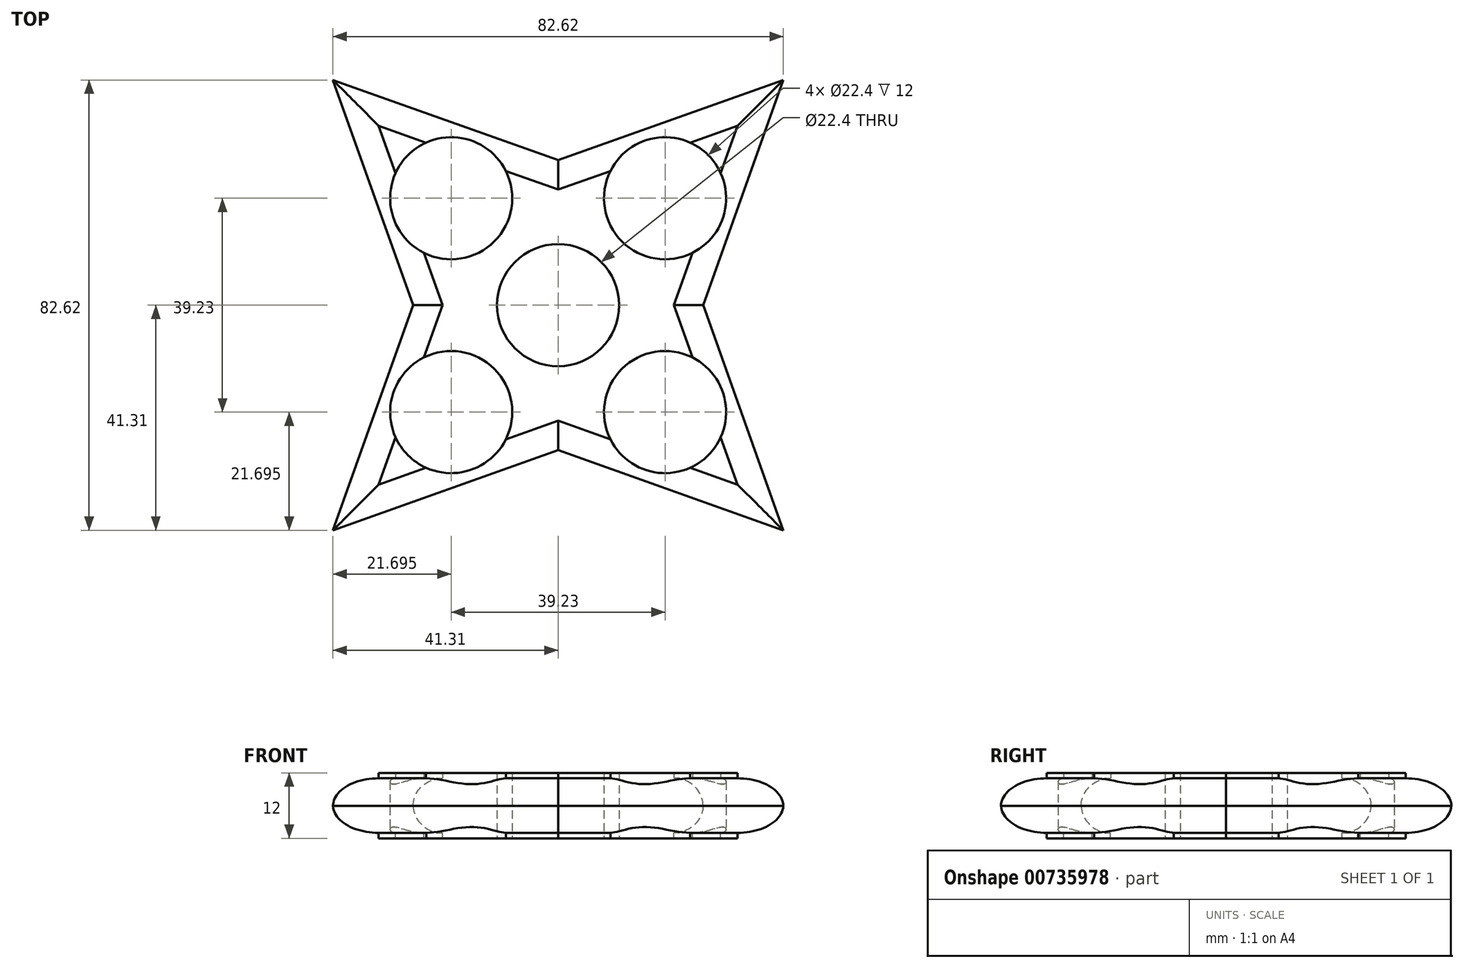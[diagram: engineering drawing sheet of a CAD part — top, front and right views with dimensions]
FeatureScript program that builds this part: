
annotation { "Feature Type Name" : "Feature", "Feature Type Description" : "" }
export const myFeature = defineFeature(function(context is Context, id is Id, definition is map)
    precondition{}
    {
        {
            var Q0;
            Q0=qCreatedBy(makeId("Top.planeOp"),FACE);
            var sketch = newSketch(context, id + "F0", { "sketchPlane" : qUnion([Q0])});
            skLineSegment(sketch, "E0.bottom", {"start": v(-109.63, 111.87) * mm, "end": v(113.44, 111.87) * mm});
            skLineSegment(sketch, "E0.top", {"start": v(-109.63, -97) * mm, "end": v(113.44, -97) * mm});
            skLineSegment(sketch, "E0.left", {"start": v(-109.63, 111.87) * mm, "end": v(-109.63, -97) * mm});
            skLineSegment(sketch, "E0.right", {"start": v(113.44, 111.87) * mm, "end": v(113.44, -97) * mm});
            skCircle(sketch, "E1", {"center": v(0, 0) * mm, "radius": 11.2 * mm});
            skLineSegment(sketch, "E2", {"start": v(0, 11.2) * mm, "end": v(0, 74.7) * mm});
            skLineSegment(sketch, "E3", {"start": v(11.2, 0) * mm, "end": v(74.7, 0) * mm});
            skLineSegment(sketch, "E4", {"start": v(0, -11.2) * mm, "end": v(0, -74.7) * mm});
            skLineSegment(sketch, "E5", {"start": v(-11.2, 0) * mm, "end": v(-74.7, 0) * mm});
            skLineSegment(sketch, "E6", {"start": v(41.3, 41.3) * mm, "end": v(0, -74.7) * mm});
            skLineSegment(sketch, "E7", {"start": v(-41.3, 41.3) * mm, "end": v(0, -74.7) * mm});
            skLineSegment(sketch, "E8", {"start": v(-74.7, 0) * mm, "end": v(41.3, 41.3) * mm});
            skLineSegment(sketch, "E9", {"start": v(41.3, -41.3) * mm, "end": v(-74.7, 0) * mm});
            skLineSegment(sketch, "E10", {"start": v(-41.3, -41.3) * mm, "end": v(0, 74.7) * mm});
            skLineSegment(sketch, "E11", {"start": v(41.3, -41.3) * mm, "end": v(0, 74.7) * mm});
            skLineSegment(sketch, "E12", {"start": v(-41.3, -41.3) * mm, "end": v(74.7, 0) * mm});
            skLineSegment(sketch, "E13", {"start": v(-41.3, 41.3) * mm, "end": v(74.7, 0) * mm});
            skLineSegment(sketch, "E14", {"start": v(0, 0) * mm, "end": v(-41.3, -41.3) * mm});
            skLineSegment(sketch, "E15", {"start": v(0, 0) * mm, "end": v(41.3, 41.3) * mm});
            skLineSegment(sketch, "E16", {"start": v(0, 0) * mm, "end": v(-41.3, 41.3) * mm});
            skLineSegment(sketch, "E17", {"start": v(0, 0) * mm, "end": v(41.3, -41.3) * mm});
            skCircle(sketch, "E18", {"center": v(-19.61, 19.61) * mm, "radius": 11.2 * mm});
            skCircle(sketch, "E19", {"center": v(19.61, 19.61) * mm, "radius": 11.2 * mm});
            skCircle(sketch, "E20", {"center": v(-19.61, -19.61) * mm, "radius": 11.2 * mm});
            skCircle(sketch, "E21", {"center": v(19.61, -19.61) * mm, "radius": 11.2 * mm});
            skSolve(sketch);
        }
        {
            var Q0;
            {var subQ0=sQuery(id+"F0.wireOp",EDGE,"E9");var subQ1=sQuery(id+"F0.wireOp",EDGE,"E6");var subQ2=makeQuery(id+"F0.imprint","INTERSECT",VERTEX,{"derivedFrom":[subQ1,subQ0]});Q0=makeQuery(id+"F0.imprint","IMPRINT",FACE,{"disambiguationData":[TD([[makeQuery(id+"F0.imprint","IMPRINT",EDGE,{"disambiguationData":[TD([[subQ2,1.0]])],"derivedFrom":subQ1}),-1.0]])]});}
            var Q1;
            {var subQ0=sQuery(id+"F0.wireOp",EDGE,"E12");var subQ1=sQuery(id+"F0.wireOp",EDGE,"E7");var subQ2=makeQuery(id+"F0.imprint","INTERSECT",VERTEX,{"derivedFrom":[subQ1,subQ0]});Q1=makeQuery(id+"F0.imprint","IMPRINT",FACE,{"disambiguationData":[TD([[makeQuery(id+"F0.imprint","IMPRINT",EDGE,{"disambiguationData":[TD([[subQ2,1.0]])],"derivedFrom":subQ1}),1.0]])]});}
            var Q2;
            {var subQ0=sQuery(id+"F0.wireOp",EDGE,"E4");var subQ1=sQuery(id+"F0.wireOp",EDGE,"E1");var subQ2=makeQuery(id+"F0.imprint","INTERSECT",VERTEX,{"derivedFrom":[subQ1,subQ0]});Q2=makeQuery(id+"F0.imprint","IMPRINT",FACE,{"disambiguationData":[TD([[makeQuery(id+"F0.imprint","IMPRINT",EDGE,{"disambiguationData":[TD([[subQ2,1.0]])],"derivedFrom":subQ1}),-1.0]])]});}
            var Q3;
            {var subQ0=sQuery(id+"F0.wireOp",EDGE,"E5");var subQ1=sQuery(id+"F0.wireOp",EDGE,"E1");var subQ2=makeQuery(id+"F0.imprint","INTERSECT",VERTEX,{"derivedFrom":[subQ1,subQ0]});Q3=makeQuery(id+"F0.imprint","IMPRINT",FACE,{"disambiguationData":[TD([[makeQuery(id+"F0.imprint","IMPRINT",EDGE,{"disambiguationData":[TD([[subQ2,-1.0]])],"derivedFrom":subQ1}),-1.0]])]});}
            var Q4;
            {var subQ0=sQuery(id+"F0.wireOp",EDGE,"E5");var subQ1=sQuery(id+"F0.wireOp",EDGE,"E1");var subQ2=makeQuery(id+"F0.imprint","INTERSECT",VERTEX,{"derivedFrom":[subQ1,subQ0]});Q4=makeQuery(id+"F0.imprint","IMPRINT",FACE,{"disambiguationData":[TD([[makeQuery(id+"F0.imprint","IMPRINT",EDGE,{"disambiguationData":[TD([[subQ2,1.0]])],"derivedFrom":subQ1}),-1.0]])]});}
            var Q5;
            {var subQ0=sQuery(id+"F0.wireOp",EDGE,"E2");var subQ1=sQuery(id+"F0.wireOp",EDGE,"E1");var subQ2=makeQuery(id+"F0.imprint","INTERSECT",VERTEX,{"derivedFrom":[subQ1,subQ0]});Q5=makeQuery(id+"F0.imprint","IMPRINT",FACE,{"disambiguationData":[TD([[makeQuery(id+"F0.imprint","IMPRINT",EDGE,{"disambiguationData":[TD([[subQ2,-1.0]])],"derivedFrom":subQ1}),-1.0]])]});}
            var Q6;
            {var subQ0=sQuery(id+"F0.wireOp",EDGE,"E2");var subQ1=sQuery(id+"F0.wireOp",EDGE,"E1");var subQ2=makeQuery(id+"F0.imprint","INTERSECT",VERTEX,{"derivedFrom":[subQ1,subQ0]});Q6=makeQuery(id+"F0.imprint","IMPRINT",FACE,{"disambiguationData":[TD([[makeQuery(id+"F0.imprint","IMPRINT",EDGE,{"disambiguationData":[TD([[subQ2,1.0]])],"derivedFrom":subQ1}),-1.0]])]});}
            var Q7;
            {var subQ0=sQuery(id+"F0.wireOp",EDGE,"E3");var subQ1=sQuery(id+"F0.wireOp",EDGE,"E1");var subQ2=makeQuery(id+"F0.imprint","INTERSECT",VERTEX,{"derivedFrom":[subQ1,subQ0]});Q7=makeQuery(id+"F0.imprint","IMPRINT",FACE,{"disambiguationData":[TD([[makeQuery(id+"F0.imprint","IMPRINT",EDGE,{"disambiguationData":[TD([[subQ2,-1.0]])],"derivedFrom":subQ1}),-1.0]])]});}
            var Q8;
            {var subQ0=sQuery(id+"F0.wireOp",EDGE,"E3");var subQ1=sQuery(id+"F0.wireOp",EDGE,"E1");var subQ2=makeQuery(id+"F0.imprint","INTERSECT",VERTEX,{"derivedFrom":[subQ1,subQ0]});Q8=makeQuery(id+"F0.imprint","IMPRINT",FACE,{"disambiguationData":[TD([[makeQuery(id+"F0.imprint","IMPRINT",EDGE,{"disambiguationData":[TD([[subQ2,1.0]])],"derivedFrom":subQ1}),-1.0]])]});}
            var Q9;
            {var subQ0=sQuery(id+"F0.wireOp",EDGE,"E4");var subQ1=sQuery(id+"F0.wireOp",EDGE,"E1");var subQ2=makeQuery(id+"F0.imprint","INTERSECT",VERTEX,{"derivedFrom":[subQ1,subQ0]});Q9=makeQuery(id+"F0.imprint","IMPRINT",FACE,{"disambiguationData":[TD([[makeQuery(id+"F0.imprint","IMPRINT",EDGE,{"disambiguationData":[TD([[subQ2,-1.0]])],"derivedFrom":subQ1}),-1.0]])]});}
            var Q10;
            {var subQ0=sQuery(id+"F0.wireOp",EDGE,"E11");var subQ3=sQuery(id+"F0.wireOp",EDGE,"E12");var subQ5=makeQuery(id+"F0.imprint","INTERSECT",VERTEX,{"derivedFrom":[subQ0,subQ3]});Q10=makeQuery(id+"F0.imprint","IMPRINT",FACE,{"disambiguationData":[TD([[makeQuery(id+"F0.imprint","IMPRINT",EDGE,{"disambiguationData":[TD([[subQ5,-1.0]])],"derivedFrom":subQ0}),1.0]])]});}
            var Q11;
            {var subQ0=sQuery(id+"F0.wireOp",EDGE,"E13");var subQ1=sQuery(id+"F0.wireOp",EDGE,"E6");var subQ2=makeQuery(id+"F0.imprint","INTERSECT",VERTEX,{"derivedFrom":[subQ1,subQ0]});Q11=makeQuery(id+"F0.imprint","IMPRINT",FACE,{"disambiguationData":[TD([[makeQuery(id+"F0.imprint","IMPRINT",EDGE,{"disambiguationData":[TD([[subQ2,-1.0]])],"derivedFrom":subQ1}),-1.0]])]});}
            var Q12;
            {var subQ0=sQuery(id+"F0.wireOp",EDGE,"E13");var subQ3=sQuery(id+"F0.wireOp",EDGE,"E10");var subQ5=makeQuery(id+"F0.imprint","INTERSECT",VERTEX,{"derivedFrom":[subQ3,subQ0]});Q12=makeQuery(id+"F0.imprint","IMPRINT",FACE,{"disambiguationData":[TD([[makeQuery(id+"F0.imprint","IMPRINT",EDGE,{"disambiguationData":[TD([[subQ5,1.0]])],"derivedFrom":subQ3}),-1.0]])]});}
            var Q13;
            {var subQ0=sQuery(id+"F0.wireOp",EDGE,"E11");var subQ1=sQuery(id+"F0.wireOp",EDGE,"E8");var subQ2=makeQuery(id+"F0.imprint","INTERSECT",VERTEX,{"derivedFrom":[subQ1,subQ0]});Q13=makeQuery(id+"F0.imprint","IMPRINT",FACE,{"disambiguationData":[TD([[makeQuery(id+"F0.imprint","IMPRINT",EDGE,{"disambiguationData":[TD([[subQ2,1.0]])],"derivedFrom":subQ1}),-1.0]])]});}
            var Q14;
            {var subQ0=sQuery(id+"F0.wireOp",EDGE,"E8");var subQ3=sQuery(id+"F0.wireOp",EDGE,"E11");var subQ5=makeQuery(id+"F0.imprint","INTERSECT",VERTEX,{"derivedFrom":[subQ0,subQ3]});Q14=makeQuery(id+"F0.imprint","IMPRINT",FACE,{"disambiguationData":[TD([[makeQuery(id+"F0.imprint","IMPRINT",EDGE,{"disambiguationData":[TD([[subQ5,-1.0]])],"derivedFrom":subQ0}),-1.0]])]});}
            var Q15;
            {var subQ0=sQuery(id+"F0.wireOp",EDGE,"E6");var subQ3=sQuery(id+"F0.wireOp",EDGE,"E13");var subQ5=makeQuery(id+"F0.imprint","INTERSECT",VERTEX,{"derivedFrom":[subQ0,subQ3]});Q15=makeQuery(id+"F0.imprint","IMPRINT",FACE,{"disambiguationData":[TD([[makeQuery(id+"F0.imprint","IMPRINT",EDGE,{"disambiguationData":[TD([[subQ5,1.0]])],"derivedFrom":subQ0}),-1.0]])]});}
            var Q16;
            {var subQ0=sQuery(id+"F0.wireOp",EDGE,"E9");var subQ3=sQuery(id+"F0.wireOp",EDGE,"E6");var subQ5=makeQuery(id+"F0.imprint","INTERSECT",VERTEX,{"derivedFrom":[subQ3,subQ0]});Q16=makeQuery(id+"F0.imprint","IMPRINT",FACE,{"disambiguationData":[TD([[makeQuery(id+"F0.imprint","IMPRINT",EDGE,{"disambiguationData":[TD([[subQ5,1.0]])],"derivedFrom":subQ3}),1.0]])]});}
            var Q17;
            {var subQ0=sQuery(id+"F0.wireOp",EDGE,"E11");var subQ3=sQuery(id+"F0.wireOp",EDGE,"E12");var subQ5=makeQuery(id+"F0.imprint","INTERSECT",VERTEX,{"derivedFrom":[subQ0,subQ3]});Q17=makeQuery(id+"F0.imprint","IMPRINT",FACE,{"disambiguationData":[TD([[makeQuery(id+"F0.imprint","IMPRINT",EDGE,{"disambiguationData":[TD([[subQ5,1.0]])],"derivedFrom":subQ0}),1.0]])]});}
            var Q18;
            {var subQ0=sQuery(id+"F0.wireOp",EDGE,"E12");var subQ3=sQuery(id+"F0.wireOp",EDGE,"E7");var subQ5=makeQuery(id+"F0.imprint","INTERSECT",VERTEX,{"derivedFrom":[subQ3,subQ0]});Q18=makeQuery(id+"F0.imprint","IMPRINT",FACE,{"disambiguationData":[TD([[makeQuery(id+"F0.imprint","IMPRINT",EDGE,{"disambiguationData":[TD([[subQ5,1.0]])],"derivedFrom":subQ3}),-1.0]])]});}
            var Q19;
            {var subQ0=sQuery(id+"F0.wireOp",EDGE,"E10");var subQ3=sQuery(id+"F0.wireOp",EDGE,"E9");var subQ5=makeQuery(id+"F0.imprint","INTERSECT",VERTEX,{"derivedFrom":[subQ3,subQ0]});Q19=makeQuery(id+"F0.imprint","IMPRINT",FACE,{"disambiguationData":[TD([[makeQuery(id+"F0.imprint","IMPRINT",EDGE,{"disambiguationData":[TD([[subQ5,1.0]])],"derivedFrom":subQ3}),-1.0]])]});}
            var Q20;
            {var subQ0=sQuery(id+"F0.wireOp",EDGE,"E10");var subQ3=sQuery(id+"F0.wireOp",EDGE,"E9");var subQ5=makeQuery(id+"F0.imprint","INTERSECT",VERTEX,{"derivedFrom":[subQ3,subQ0]});Q20=makeQuery(id+"F0.imprint","IMPRINT",FACE,{"disambiguationData":[TD([[makeQuery(id+"F0.imprint","IMPRINT",EDGE,{"disambiguationData":[TD([[subQ5,1.0]])],"derivedFrom":subQ3}),1.0]])]});}
            var Q21;
            {var subQ0=sQuery(id+"F0.wireOp",EDGE,"E8");var subQ1=sQuery(id+"F0.wireOp",EDGE,"E7");var subQ2=makeQuery(id+"F0.imprint","INTERSECT",VERTEX,{"derivedFrom":[subQ1,subQ0]});Q21=makeQuery(id+"F0.imprint","IMPRINT",FACE,{"disambiguationData":[TD([[makeQuery(id+"F0.imprint","IMPRINT",EDGE,{"disambiguationData":[TD([[subQ2,-1.0]])],"derivedFrom":subQ1}),1.0]])]});}
            var Q22;
            {var subQ0=sQuery(id+"F0.wireOp",EDGE,"E7");var subQ3=sQuery(id+"F0.wireOp",EDGE,"E8");var subQ5=makeQuery(id+"F0.imprint","INTERSECT",VERTEX,{"derivedFrom":[subQ0,subQ3]});Q22=makeQuery(id+"F0.imprint","IMPRINT",FACE,{"disambiguationData":[TD([[makeQuery(id+"F0.imprint","IMPRINT",EDGE,{"disambiguationData":[TD([[subQ5,1.0]])],"derivedFrom":subQ0}),1.0]])]});}
            var Q23;
            {var subQ0=sQuery(id+"F0.wireOp",EDGE,"E13");var subQ3=sQuery(id+"F0.wireOp",EDGE,"E10");var subQ5=makeQuery(id+"F0.imprint","INTERSECT",VERTEX,{"derivedFrom":[subQ3,subQ0]});Q23=makeQuery(id+"F0.imprint","IMPRINT",FACE,{"disambiguationData":[TD([[makeQuery(id+"F0.imprint","IMPRINT",EDGE,{"disambiguationData":[TD([[subQ5,1.0]])],"derivedFrom":subQ3}),1.0]])]});}
            extrude(context, id + "F1", {"entities" : qUnion([Q0, Q1, Q2, Q3, Q4, Q5, Q6, Q7, Q8, Q9, Q10, Q11, Q12, Q13, Q14, Q15, Q16, Q17, Q18, Q19, Q20, Q21, Q22, Q23]), "depth" : 10 * mm, "offsetDistance" : 25.4 * mm});
        }
        {
            var Q0;
            Q0=makeQuery(id+"F1.opExtrude","CAP_EDGE",EDGE,{"disambiguationData":[OSD([sQuery(id+"F0.wireOp",EDGE,"E10")])],"isStart":false});
            var Q1;
            Q1=makeQuery(id+"F1.opExtrude","CAP_EDGE",EDGE,{"disambiguationData":[OSD([sQuery(id+"F0.wireOp",EDGE,"E7")])],"isStart":false});
            var Q2;
            Q2=makeQuery(id+"F1.opExtrude","CAP_EDGE",EDGE,{"disambiguationData":[OSD([sQuery(id+"F0.wireOp",EDGE,"E12")])],"isStart":false});
            var Q3;
            Q3=makeQuery(id+"F1.opExtrude","CAP_EDGE",EDGE,{"disambiguationData":[OSD([sQuery(id+"F0.wireOp",EDGE,"E9")])],"isStart":false});
            var Q4;
            Q4=makeQuery(id+"F1.opExtrude","CAP_EDGE",EDGE,{"disambiguationData":[OSD([sQuery(id+"F0.wireOp",EDGE,"E11")])],"isStart":false});
            var Q5;
            Q5=makeQuery(id+"F1.opExtrude","CAP_EDGE",EDGE,{"disambiguationData":[OSD([sQuery(id+"F0.wireOp",EDGE,"E6")])],"isStart":false});
            var Q6;
            Q6=makeQuery(id+"F1.opExtrude","CAP_EDGE",EDGE,{"disambiguationData":[OSD([sQuery(id+"F0.wireOp",EDGE,"E8")])],"isStart":false});
            var Q7;
            Q7=makeQuery(id+"F1.opExtrude","CAP_EDGE",EDGE,{"disambiguationData":[OSD([sQuery(id+"F0.wireOp",EDGE,"E13")])],"isStart":false});
            fillet(context, id + "F2", {"entities" : qUnion([Q0, Q1, Q2, Q3, Q4, Q5, Q6, Q7]), "radius" : 5.08 * mm, "tangentPropagation" : true, "allowEdgeOverflow" : false});
        }
        {
            var Q0;
            Q0=makeQuery(id+"F1.opExtrude","CAP_EDGE",EDGE,{"disambiguationData":[OSD([sQuery(id+"F0.wireOp",EDGE,"E8")])],"isStart":true});
            var Q1;
            Q1=makeQuery(id+"F1.opExtrude","CAP_EDGE",EDGE,{"disambiguationData":[OSD([sQuery(id+"F0.wireOp",EDGE,"E6")])],"isStart":true});
            var Q2;
            Q2=makeQuery(id+"F1.opExtrude","CAP_EDGE",EDGE,{"disambiguationData":[OSD([sQuery(id+"F0.wireOp",EDGE,"E11")])],"isStart":true});
            var Q3;
            Q3=makeQuery(id+"F1.opExtrude","CAP_EDGE",EDGE,{"disambiguationData":[OSD([sQuery(id+"F0.wireOp",EDGE,"E9")])],"isStart":true});
            var Q4;
            Q4=makeQuery(id+"F1.opExtrude","CAP_EDGE",EDGE,{"disambiguationData":[OSD([sQuery(id+"F0.wireOp",EDGE,"E12")])],"isStart":true});
            var Q5;
            Q5=makeQuery(id+"F1.opExtrude","CAP_EDGE",EDGE,{"disambiguationData":[OSD([sQuery(id+"F0.wireOp",EDGE,"E10")])],"isStart":true});
            var Q6;
            Q6=makeQuery(id+"F1.opExtrude","CAP_EDGE",EDGE,{"disambiguationData":[OSD([sQuery(id+"F0.wireOp",EDGE,"E7")])],"isStart":true});
            var Q7;
            Q7=makeQuery(id+"F1.opExtrude","CAP_EDGE",EDGE,{"disambiguationData":[OSD([sQuery(id+"F0.wireOp",EDGE,"E13")])],"isStart":true});
            fillet(context, id + "F3", {"entities" : qUnion([Q0, Q1, Q2, Q3, Q4, Q5, Q6, Q7]), "radius" : 5.08 * mm, "tangentPropagation" : true, "allowEdgeOverflow" : false});
        }
        {
            var Q0;
            Q0=makeQuery(id+"F2.opFillet","SPLIT",FACE,{"disambiguationData":[OD(2.0)],"derivedFrom":makeQuery(id+"F1.opExtrude","CAP_FACE",FACE,{"disambiguationData":[OSD([sQuery(id+"F0.wireOp",EDGE,"E1"),sQuery(id+"F0.wireOp",EDGE,"E6"),sQuery(id+"F0.wireOp",EDGE,"E7"),sQuery(id+"F0.wireOp",EDGE,"E8"),sQuery(id+"F0.wireOp",EDGE,"E9"),sQuery(id+"F0.wireOp",EDGE,"E10"),sQuery(id+"F0.wireOp",EDGE,"E11"),sQuery(id+"F0.wireOp",EDGE,"E12"),sQuery(id+"F0.wireOp",EDGE,"E13"),sQuery(id+"F0.wireOp",EDGE,"NQLChufh-tOBQ-VhrW-I5os-LazHDcaticKj"),sQuery(id+"F0.wireOp",EDGE,"nPcMzMfi-i0d1-RiFT-5sVm-fAcf6640eUi0"),sQuery(id+"F0.wireOp",EDGE,"xpLk3V2d-4zdc-2TxM-j6uB-WA1YDWCwNWJT"),sQuery(id+"F0.wireOp",EDGE,"mvu3pI7v-0WKY-5XG3-tPVA-ciItBbTbTf2v")])],"isStart":false})});
            var Q1;
            Q1=makeQuery(id+"F2.opFillet","SPLIT",FACE,{"disambiguationData":[OD(1.0)],"derivedFrom":makeQuery(id+"F1.opExtrude","CAP_FACE",FACE,{"disambiguationData":[OSD([sQuery(id+"F0.wireOp",EDGE,"E1"),sQuery(id+"F0.wireOp",EDGE,"E6"),sQuery(id+"F0.wireOp",EDGE,"E7"),sQuery(id+"F0.wireOp",EDGE,"E8"),sQuery(id+"F0.wireOp",EDGE,"E9"),sQuery(id+"F0.wireOp",EDGE,"E10"),sQuery(id+"F0.wireOp",EDGE,"E11"),sQuery(id+"F0.wireOp",EDGE,"E12"),sQuery(id+"F0.wireOp",EDGE,"E13"),sQuery(id+"F0.wireOp",EDGE,"NQLChufh-tOBQ-VhrW-I5os-LazHDcaticKj"),sQuery(id+"F0.wireOp",EDGE,"nPcMzMfi-i0d1-RiFT-5sVm-fAcf6640eUi0"),sQuery(id+"F0.wireOp",EDGE,"xpLk3V2d-4zdc-2TxM-j6uB-WA1YDWCwNWJT"),sQuery(id+"F0.wireOp",EDGE,"mvu3pI7v-0WKY-5XG3-tPVA-ciItBbTbTf2v")])],"isStart":false})});
            var Q2;
            Q2=makeQuery(id+"F2.opFillet","SPLIT",FACE,{"disambiguationData":[OD(3.0)],"derivedFrom":makeQuery(id+"F1.opExtrude","CAP_FACE",FACE,{"disambiguationData":[OSD([sQuery(id+"F0.wireOp",EDGE,"E1"),sQuery(id+"F0.wireOp",EDGE,"E6"),sQuery(id+"F0.wireOp",EDGE,"E7"),sQuery(id+"F0.wireOp",EDGE,"E8"),sQuery(id+"F0.wireOp",EDGE,"E9"),sQuery(id+"F0.wireOp",EDGE,"E10"),sQuery(id+"F0.wireOp",EDGE,"E11"),sQuery(id+"F0.wireOp",EDGE,"E12"),sQuery(id+"F0.wireOp",EDGE,"E13"),sQuery(id+"F0.wireOp",EDGE,"NQLChufh-tOBQ-VhrW-I5os-LazHDcaticKj"),sQuery(id+"F0.wireOp",EDGE,"nPcMzMfi-i0d1-RiFT-5sVm-fAcf6640eUi0"),sQuery(id+"F0.wireOp",EDGE,"xpLk3V2d-4zdc-2TxM-j6uB-WA1YDWCwNWJT"),sQuery(id+"F0.wireOp",EDGE,"mvu3pI7v-0WKY-5XG3-tPVA-ciItBbTbTf2v")])],"isStart":false})});
            var Q3;
            Q3=makeQuery(id+"F2.opFillet","SPLIT",FACE,{"disambiguationData":[OD(0.0)],"derivedFrom":makeQuery(id+"F1.opExtrude","CAP_FACE",FACE,{"disambiguationData":[OSD([sQuery(id+"F0.wireOp",EDGE,"E1"),sQuery(id+"F0.wireOp",EDGE,"E6"),sQuery(id+"F0.wireOp",EDGE,"E7"),sQuery(id+"F0.wireOp",EDGE,"E8"),sQuery(id+"F0.wireOp",EDGE,"E9"),sQuery(id+"F0.wireOp",EDGE,"E10"),sQuery(id+"F0.wireOp",EDGE,"E11"),sQuery(id+"F0.wireOp",EDGE,"E12"),sQuery(id+"F0.wireOp",EDGE,"E13"),sQuery(id+"F0.wireOp",EDGE,"NQLChufh-tOBQ-VhrW-I5os-LazHDcaticKj"),sQuery(id+"F0.wireOp",EDGE,"nPcMzMfi-i0d1-RiFT-5sVm-fAcf6640eUi0"),sQuery(id+"F0.wireOp",EDGE,"xpLk3V2d-4zdc-2TxM-j6uB-WA1YDWCwNWJT"),sQuery(id+"F0.wireOp",EDGE,"mvu3pI7v-0WKY-5XG3-tPVA-ciItBbTbTf2v")])],"isStart":false})});
            var Q4;
            Q4=makeQuery(id+"F2.opFillet","SPLIT",FACE,{"disambiguationData":[OD(4.0)],"derivedFrom":makeQuery(id+"F1.opExtrude","CAP_FACE",FACE,{"disambiguationData":[OSD([sQuery(id+"F0.wireOp",EDGE,"E1"),sQuery(id+"F0.wireOp",EDGE,"E6"),sQuery(id+"F0.wireOp",EDGE,"E7"),sQuery(id+"F0.wireOp",EDGE,"E8"),sQuery(id+"F0.wireOp",EDGE,"E9"),sQuery(id+"F0.wireOp",EDGE,"E10"),sQuery(id+"F0.wireOp",EDGE,"E11"),sQuery(id+"F0.wireOp",EDGE,"E12"),sQuery(id+"F0.wireOp",EDGE,"E13"),sQuery(id+"F0.wireOp",EDGE,"NQLChufh-tOBQ-VhrW-I5os-LazHDcaticKj"),sQuery(id+"F0.wireOp",EDGE,"nPcMzMfi-i0d1-RiFT-5sVm-fAcf6640eUi0"),sQuery(id+"F0.wireOp",EDGE,"xpLk3V2d-4zdc-2TxM-j6uB-WA1YDWCwNWJT"),sQuery(id+"F0.wireOp",EDGE,"mvu3pI7v-0WKY-5XG3-tPVA-ciItBbTbTf2v")])],"isStart":false})});
            extrude(context, id + "F4", {"entities" : qUnion([Q0, Q1, Q2, Q3, Q4]), "operationType" : NewBodyOperationType.ADD, "depth" : 1 * mm, "offsetDistance" : 25.4 * mm});
        }
        {
            var Q0;
            Q0=makeQuery(id+"F3.opFillet","SPLIT",FACE,{"disambiguationData":[OD(2.0)],"derivedFrom":makeQuery(id+"F1.opExtrude","CAP_FACE",FACE,{"disambiguationData":[OSD([sQuery(id+"F0.wireOp",EDGE,"E1"),sQuery(id+"F0.wireOp",EDGE,"E6"),sQuery(id+"F0.wireOp",EDGE,"E7"),sQuery(id+"F0.wireOp",EDGE,"E8"),sQuery(id+"F0.wireOp",EDGE,"E9"),sQuery(id+"F0.wireOp",EDGE,"E10"),sQuery(id+"F0.wireOp",EDGE,"E11"),sQuery(id+"F0.wireOp",EDGE,"E12"),sQuery(id+"F0.wireOp",EDGE,"E13"),sQuery(id+"F0.wireOp",EDGE,"NQLChufh-tOBQ-VhrW-I5os-LazHDcaticKj"),sQuery(id+"F0.wireOp",EDGE,"nPcMzMfi-i0d1-RiFT-5sVm-fAcf6640eUi0"),sQuery(id+"F0.wireOp",EDGE,"xpLk3V2d-4zdc-2TxM-j6uB-WA1YDWCwNWJT"),sQuery(id+"F0.wireOp",EDGE,"mvu3pI7v-0WKY-5XG3-tPVA-ciItBbTbTf2v")])],"isStart":true})});
            var Q1;
            Q1=makeQuery(id+"F3.opFillet","SPLIT",FACE,{"disambiguationData":[OD(3.0)],"derivedFrom":makeQuery(id+"F1.opExtrude","CAP_FACE",FACE,{"disambiguationData":[OSD([sQuery(id+"F0.wireOp",EDGE,"E1"),sQuery(id+"F0.wireOp",EDGE,"E6"),sQuery(id+"F0.wireOp",EDGE,"E7"),sQuery(id+"F0.wireOp",EDGE,"E8"),sQuery(id+"F0.wireOp",EDGE,"E9"),sQuery(id+"F0.wireOp",EDGE,"E10"),sQuery(id+"F0.wireOp",EDGE,"E11"),sQuery(id+"F0.wireOp",EDGE,"E12"),sQuery(id+"F0.wireOp",EDGE,"E13"),sQuery(id+"F0.wireOp",EDGE,"NQLChufh-tOBQ-VhrW-I5os-LazHDcaticKj"),sQuery(id+"F0.wireOp",EDGE,"nPcMzMfi-i0d1-RiFT-5sVm-fAcf6640eUi0"),sQuery(id+"F0.wireOp",EDGE,"xpLk3V2d-4zdc-2TxM-j6uB-WA1YDWCwNWJT"),sQuery(id+"F0.wireOp",EDGE,"mvu3pI7v-0WKY-5XG3-tPVA-ciItBbTbTf2v")])],"isStart":true})});
            var Q2;
            Q2=makeQuery(id+"F3.opFillet","SPLIT",FACE,{"disambiguationData":[OD(0.0)],"derivedFrom":makeQuery(id+"F1.opExtrude","CAP_FACE",FACE,{"disambiguationData":[OSD([sQuery(id+"F0.wireOp",EDGE,"E1"),sQuery(id+"F0.wireOp",EDGE,"E6"),sQuery(id+"F0.wireOp",EDGE,"E7"),sQuery(id+"F0.wireOp",EDGE,"E8"),sQuery(id+"F0.wireOp",EDGE,"E9"),sQuery(id+"F0.wireOp",EDGE,"E10"),sQuery(id+"F0.wireOp",EDGE,"E11"),sQuery(id+"F0.wireOp",EDGE,"E12"),sQuery(id+"F0.wireOp",EDGE,"E13"),sQuery(id+"F0.wireOp",EDGE,"NQLChufh-tOBQ-VhrW-I5os-LazHDcaticKj"),sQuery(id+"F0.wireOp",EDGE,"nPcMzMfi-i0d1-RiFT-5sVm-fAcf6640eUi0"),sQuery(id+"F0.wireOp",EDGE,"xpLk3V2d-4zdc-2TxM-j6uB-WA1YDWCwNWJT"),sQuery(id+"F0.wireOp",EDGE,"mvu3pI7v-0WKY-5XG3-tPVA-ciItBbTbTf2v")])],"isStart":true})});
            var Q3;
            Q3=makeQuery(id+"F3.opFillet","SPLIT",FACE,{"disambiguationData":[OD(1.0)],"derivedFrom":makeQuery(id+"F1.opExtrude","CAP_FACE",FACE,{"disambiguationData":[OSD([sQuery(id+"F0.wireOp",EDGE,"E1"),sQuery(id+"F0.wireOp",EDGE,"E6"),sQuery(id+"F0.wireOp",EDGE,"E7"),sQuery(id+"F0.wireOp",EDGE,"E8"),sQuery(id+"F0.wireOp",EDGE,"E9"),sQuery(id+"F0.wireOp",EDGE,"E10"),sQuery(id+"F0.wireOp",EDGE,"E11"),sQuery(id+"F0.wireOp",EDGE,"E12"),sQuery(id+"F0.wireOp",EDGE,"E13"),sQuery(id+"F0.wireOp",EDGE,"NQLChufh-tOBQ-VhrW-I5os-LazHDcaticKj"),sQuery(id+"F0.wireOp",EDGE,"nPcMzMfi-i0d1-RiFT-5sVm-fAcf6640eUi0"),sQuery(id+"F0.wireOp",EDGE,"xpLk3V2d-4zdc-2TxM-j6uB-WA1YDWCwNWJT"),sQuery(id+"F0.wireOp",EDGE,"mvu3pI7v-0WKY-5XG3-tPVA-ciItBbTbTf2v")])],"isStart":true})});
            var Q4;
            Q4=makeQuery(id+"F3.opFillet","SPLIT",FACE,{"disambiguationData":[OD(4.0)],"derivedFrom":makeQuery(id+"F1.opExtrude","CAP_FACE",FACE,{"disambiguationData":[OSD([sQuery(id+"F0.wireOp",EDGE,"E1"),sQuery(id+"F0.wireOp",EDGE,"E6"),sQuery(id+"F0.wireOp",EDGE,"E7"),sQuery(id+"F0.wireOp",EDGE,"E8"),sQuery(id+"F0.wireOp",EDGE,"E9"),sQuery(id+"F0.wireOp",EDGE,"E10"),sQuery(id+"F0.wireOp",EDGE,"E11"),sQuery(id+"F0.wireOp",EDGE,"E12"),sQuery(id+"F0.wireOp",EDGE,"E13"),sQuery(id+"F0.wireOp",EDGE,"NQLChufh-tOBQ-VhrW-I5os-LazHDcaticKj"),sQuery(id+"F0.wireOp",EDGE,"nPcMzMfi-i0d1-RiFT-5sVm-fAcf6640eUi0"),sQuery(id+"F0.wireOp",EDGE,"xpLk3V2d-4zdc-2TxM-j6uB-WA1YDWCwNWJT"),sQuery(id+"F0.wireOp",EDGE,"mvu3pI7v-0WKY-5XG3-tPVA-ciItBbTbTf2v")])],"isStart":true})});
            extrude(context, id + "F5", {"entities" : qUnion([Q0, Q1, Q2, Q3, Q4]), "operationType" : NewBodyOperationType.ADD, "depth" : 1 * mm, "offsetDistance" : 25.4 * mm});
        }
    });
